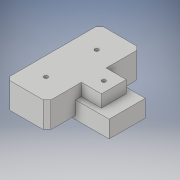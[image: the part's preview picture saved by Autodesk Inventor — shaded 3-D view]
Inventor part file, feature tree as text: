
AUTODESK INVENTOR PART (.ipt)
format: ipt  version: 2019 (Build 230136000, 136)  size: 366,592 bytes
history: native  units: mm
features: extrude x11, sketch x11, direct_edit x2, chamfer x2, move_body x2
ambient origin geometry x8: Origin, YZ Plane, XZ Plane, XY Plane, X Axis, Y Axis, Z Axis, Center Point
bodies: Solid1 (feature_tree)
feature tree (28):
  extrude  "Extrusion1"  Depth=19.0mm
  extrude  "Extrusion2"  Depth=10.5mm
  extrude  "Extrusion3"  Depth=3.0mm TaperAngle=0.0deg
  extrude  "Extrusion4"  Depth=10.0mm TaperAngle=0.0deg
  extrude  "Extrusion5"  Depth=15.0mm TaperAngle=0.0deg
  direct_edit  "Direct Edit1"
  extrude  "Extrusion6"  Depth=6.5mm
  extrude  "Extrusion7"  Depth=2.0mm
  sketch  "Sketch8"  dims[d21=3.0mm d22=0.0mm d23=1.0mm]
  extrude  "Extrusion8"  Depth=1.0mm
  extrude  "Extrusion9"  Depth=1.0mm
  direct_edit  "Direct Edit2"
  extrude  "Extrusion10"  Depth=6.0mm TaperAngle=0.0deg
  extrude  "Extrusion11"  Depth=3.5mm TaperAngle=0.0deg
  chamfer  "Chamfer1"  Distance=2.0mm
  chamfer  "Chamfer2"  Distance=2.0mm
  sketch  "Sketch1"  dims[d0=17.5mm d1=19.0mm]
  sketch  "Sketch2"  dims[d2=9.0mm d3=0.0mm d4=10.5mm]
  sketch  "Sketch3"  dims[d5=13.0mm d6=3.0mm d7=0.0mm]
  sketch  "Sketch4"  dims[d8=1.0mm d9=0.0mm d10=10.0mm d11=0.0mm]
  sketch  "Sketch5"  dims[d12=49.0mm d13=15.0mm d14=0.0mm]
  sketch  "Sketch6"  dims[d15=0.0mm d16=0.0mm d17=6.5mm d18=2.0mm]
  sketch  "Sketch7"  dims[d19=2.0mm d20=2.0mm]
  sketch  "Sketch9"  dims[d24=1.0mm d25=1.0mm]
  sketch  "Sketch10"  dims[d26=3.0mm d27=0.0mm d29=6.0mm d30=0.0mm]
  sketch  "Sketch11"  dims[d31=3.0mm d32=0.0mm d33=0.0mm d34=0.0mm d35=3.5mm d36=2.0mm d37=2.0mm d38=2.0mm d39=3.0mm d40=0.0mm d41=1.0mm d42=1.0mm d43=1.0mm d44=3.0mm d45=0.0mm d46=2.0mm d47=2.0mm d48=45.0deg d49=2.0mm d50=2.0mm d51=45.0deg]
  move_body  "Move1"
  move_body  "Move2"
